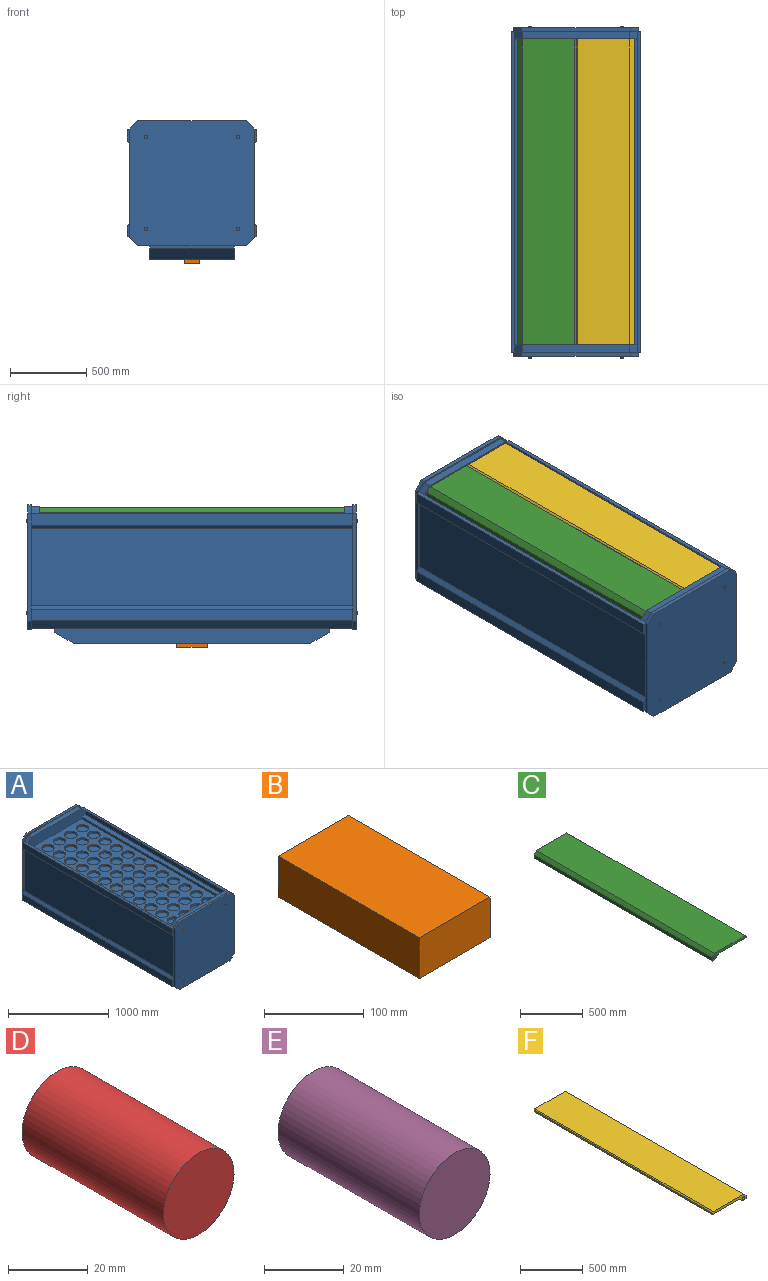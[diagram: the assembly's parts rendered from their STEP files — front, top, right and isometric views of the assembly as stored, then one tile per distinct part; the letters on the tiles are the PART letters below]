
ASSEMBLY  parts=6 mates=5
PART A: 218 faces, bbox 850x2170x910 mm
  f0: plane 1540.19x550mm, normal (0,0,-1), area 827105.8mm2, adj f28,f29,f30,f129,f213,f214,f215,f216
  f1: plane 820x60mm, normal (0,1,0), area 8579.9mm2, adj f11,f13,f14,f15,f16,f65,f122,f123
  f2: plane 520x10mm, normal (0,-1,0), area 5100mm2, adj f5,f24,f67,f68
  f3: plane 520x10mm, normal (0,1,0), area 5100mm2, adj f5,f16,f67,f68
  f4: plane 820x60mm, normal (0,-1,0), area 8579.9mm2, adj f10,f12,f22,f23,f24,f61,f121,f126
  f5: plane 2100x500mm, normal (1,0,0), area 1050000mm2, adj f2,f3,f67,f68
  f6: plane 700x50mm, normal (0,0,1), area 35000mm2, adj f7,f19,f53,f120
  f7: plane 50x50mm, normal (0.71,0,0.71), area 3535.5mm2, adj f6,f19,f53,f61
  f8: plane 820x820mm, normal (0,1,0), area 664559.8mm2, adj f21,f22,f23,f24,f25,f41,f42,f43
  f9: plane 820x820mm, normal (0,-1,0), area 664559.8mm2, adj f14,f15,f16,f17,f18,f31,f32,f33
  f10: plane 700x50mm, normal (0,0,1), area 35000mm2, adj f4,f12,f51,f121
  f11: plane 2100x700mm, normal (0,0,-1), area 480000mm2, adj f1,f13,f20,f26,f27,f28,f122,f129
  f12: plane 50x50mm, normal (0.71,0,0.71), area 3535.5mm2, adj f4,f10,f51,f61
  f13: plane 2100x50mm, normal (0.71,0,-0.71), area 148492.4mm2, adj f1,f11,f20,f65
  f14: plane 708.28x25mm, normal (0,0,-1), area 17707.1mm2, adj f1,f9,f15,f123
  f15: plane 55.86x55.86mm, normal (0.71,0,-0.71), area 1974.9mm2, adj f1,f9,f14,f16
  f16: plane 708.28x25mm, normal (1,0,0), area 17707.1mm2, adj f1,f3,f9,f15,f17,f19,f58,f64
  f17: plane 55.86x55.86mm, normal (0.71,0,0.71), area 1974.9mm2, adj f9,f16,f18,f19
  f18: plane 708.28x25mm, normal (0,0,1), area 17707.1mm2, adj f9,f17,f19,f125
  f19: plane 820x60mm, normal (0,1,0), area 8579.9mm2, adj f6,f7,f16,f17,f18,f61,f120,f124
  f20: plane 820x60mm, normal (0,-1,0), area 8579.9mm2, adj f11,f13,f21,f24,f25,f65,f122,f127
  f21: plane 708.28x25mm, normal (0,0,-1), area 17707.1mm2, adj f8,f20,f25,f128
  f22: plane 708.28x25mm, normal (0,0,1), area 17707.1mm2, adj f4,f8,f23,f126
  f23: plane 55.86x55.86mm, normal (0.71,0,0.71), area 1974.9mm2, adj f4,f8,f22,f24
  f24: plane 708.28x25mm, normal (1,0,0), area 17707.1mm2, adj f2,f4,f8,f20,f23,f25,f59,f63
  f25: plane 55.86x55.86mm, normal (0.71,0,-0.71), area 1974.9mm2, adj f8,f20,f21,f24
  f26: plane 550x25mm, normal (0,-1,0), area 13750mm2, adj f11,f28,f30,f129
  f27: plane 550x25mm, normal (0,1,0), area 13750mm2, adj f11,f28,f29,f129
  f28: plane 1800x100mm, normal (1,0,0), area 170257.2mm2, adj f0,f11,f26,f27,f29,f30
  f29: plane 550x129.9mm, normal (0,0.5,-0.87), area 82500mm2, adj f0,f27,f28,f129
  f30: plane 550x129.9mm, normal (0,-0.5,-0.87), area 82500mm2, adj f0,f26,f28,f129
  f31: plane 20x10mm, normal (0,0,1), area 200mm2, adj f9,f32,f34,f35
  f32: plane 20x10mm, normal (-1,0,0), area 200mm2, adj f9,f31,f33,f35
  f33: plane 20x10mm, normal (0,0,-1), area 200mm2, adj f9,f32,f34,f35
  f34: plane 20x10mm, normal (1,0,0), area 200mm2, adj f9,f31,f33,f35
  f35: plane 20x20mm, normal (0,-1,0), area 400mm2, adj f31,f32,f33,f34
  f36: plane 20x10mm, normal (0,0,1), area 200mm2, adj f9,f37,f39,f40
  f37: plane 20x10mm, normal (-1,0,0), area 200mm2, adj f9,f36,f38,f40
  f38: plane 20x10mm, normal (0,0,-1), area 200mm2, adj f9,f37,f39,f40
  f39: plane 20x10mm, normal (1,0,0), area 200mm2, adj f9,f36,f38,f40
  f40: plane 20x20mm, normal (0,-1,0), area 400mm2, adj f36,f37,f38,f39
  f41: plane 20x10mm, normal (0,0,1), area 200mm2, adj f8,f42,f44,f45
  f42: plane 20x10mm, normal (1,0,0), area 200mm2, adj f8,f41,f43,f45
  f43: plane 20x10mm, normal (0,0,-1), area 200mm2, adj f8,f42,f44,f45
  f44: plane 20x10mm, normal (-1,0,0), area 200mm2, adj f8,f41,f43,f45
  f45: plane 20x20mm, normal (0,1,0), area 400mm2, adj f41,f42,f43,f44
  f46: plane 20x10mm, normal (0,0,1), area 200mm2, adj f8,f47,f49,f50
  f47: plane 20x10mm, normal (1,0,0), area 200mm2, adj f8,f46,f48,f50
  f48: plane 20x10mm, normal (0,0,-1), area 200mm2, adj f8,f47,f49,f50
  f49: plane 20x10mm, normal (-1,0,0), area 200mm2, adj f8,f46,f48,f50
  f50: plane 20x20mm, normal (0,1,0), area 400mm2, adj f46,f47,f48,f49
  f51: plane 800x125mm, normal (0,-1,0), area 95000mm2, adj f10,f12,f52,f54,f55,f60,f121,f150
  f52: plane 2000x50mm, normal (0,0,1), area 100000mm2, adj f51,f53,f54,f60
  f53: plane 800x125mm, normal (0,1,0), area 94018.3mm2, adj f6,f7,f52,f54,f55,f56,f60,f120
  f54: plane 2000x25mm, normal (-1,0,0), area 50000mm2, adj f51,f52,f53,f55
  f55: plane 2000x700mm, normal (0,0,1), area 810951.4mm2, adj f51,f53,f54,f69,f71,f73,f75,f77
  f56: cylinder r=12.5mm len=25mm, axis (0,1,0), area 1963.5mm2, adj f53,f57
  f57: plane 25x25mm, normal (0,1,0), area 490.9mm2, adj f56
  f58: plane 90x15mm, normal (0,-1,0), area 1237.5mm2, adj f16,f61,f62,f68
  f59: plane 90x15mm, normal (0,1,0), area 1237.5mm2, adj f24,f61,f62,f68
  f60: plane 2000x50mm, normal (-1,0,0), area 100000mm2, adj f51,f52,f53,f61
  f61: plane 2100x25mm, normal (0,0,1), area 52500mm2, adj f4,f7,f12,f19,f58,f59,f60,f62
  f62: plane 2100x75mm, normal (1,0,0), area 157500mm2, adj f58,f59,f61,f68
  f63: plane 90x15mm, normal (0,1,0), area 1237.5mm2, adj f24,f65,f66,f67
  f64: plane 90x15mm, normal (0,-1,0), area 1237.5mm2, adj f16,f65,f66,f67
  f65: plane 2100x25mm, normal (0,0,-1), area 52500mm2, adj f1,f13,f20,f63,f64,f66
  f66: plane 2100x75mm, normal (1,0,0), area 157500mm2, adj f63,f64,f65,f67
  f67: plane 2100x25mm, normal (0.71,0,0.71), area 74246.2mm2, adj f2,f3,f5,f63,f64,f66
  f68: plane 2100x25mm, normal (0.71,0,-0.71), area 74246.2mm2, adj f2,f3,f5,f58,f59,f62
  f69: cylinder r=62.5mm len=125mm, axis (0,0,1), area 9817.5mm2, adj f55,f70
  f70: plane 125x125mm, normal (0,0,1), area 12271.8mm2, adj f69
  f71: cylinder r=62.5mm len=125mm, axis (0,0,1), area 9817.5mm2, adj f55,f72
  f72: plane 125x125mm, normal (0,0,1), area 12271.8mm2, adj f71
  f73: cylinder r=62.5mm len=125mm, axis (0,0,1), area 9817.5mm2, adj f55,f74
  f74: plane 125x125mm, normal (0,0,1), area 12271.8mm2, adj f73
  f75: cylinder r=62.5mm len=125mm, axis (0,0,1), area 9817.5mm2, adj f55,f76
  f76: plane 125x125mm, normal (0,0,1), area 12271.8mm2, adj f75
  f77: cylinder r=62.5mm len=125mm, axis (0,0,1), area 9817.5mm2, adj f55,f78
  f78: plane 125x125mm, normal (0,0,1), area 12271.8mm2, adj f77
  f79: cylinder r=62.5mm len=125mm, axis (0,0,1), area 9817.5mm2, adj f55,f80
  f80: plane 125x125mm, normal (0,0,1), area 12271.8mm2, adj f79
  f81: cylinder r=62.5mm len=125mm, axis (0,0,1), area 9817.5mm2, adj f55,f82
  f82: plane 125x125mm, normal (0,0,1), area 12271.8mm2, adj f81
  f83: cylinder r=62.5mm len=125mm, axis (0,0,1), area 9817.5mm2, adj f55,f84
  f84: plane 125x125mm, normal (0,0,1), area 12271.8mm2, adj f83
  f85: cylinder r=62.5mm len=125mm, axis (0,0,1), area 9817.5mm2, adj f55,f86
  f86: plane 125x125mm, normal (0,0,1), area 12271.8mm2, adj f85
  f87: cylinder r=62.5mm len=125mm, axis (0,0,1), area 9817.5mm2, adj f55,f88
  f88: plane 125x125mm, normal (0,0,1), area 12271.8mm2, adj f87
  f89: cylinder r=62.5mm len=125mm, axis (0,0,1), area 9817.5mm2, adj f55,f90
  f90: plane 125x125mm, normal (0,0,1), area 12271.8mm2, adj f89
  f91: cylinder r=62.5mm len=125mm, axis (0,0,1), area 9817.5mm2, adj f55,f92
  f92: plane 125x125mm, normal (0,0,1), area 12271.8mm2, adj f91
  f93: cylinder r=62.5mm len=125mm, axis (0,0,1), area 9817.5mm2, adj f55,f94
  f94: plane 125x125mm, normal (0,0,1), area 12271.8mm2, adj f93
  f95: cylinder r=62.5mm len=125mm, axis (0,0,1), area 9817.5mm2, adj f55,f96
  f96: plane 125x125mm, normal (0,0,1), area 12271.8mm2, adj f95
  f97: cylinder r=62.5mm len=125mm, axis (0,0,1), area 9817.5mm2, adj f55,f98
  f98: plane 125x125mm, normal (0,0,1), area 12271.8mm2, adj f97
  f99: cylinder r=62.5mm len=125mm, axis (0,0,1), area 9817.5mm2, adj f55,f100
  f100: plane 125x125mm, normal (0,0,1), area 12271.8mm2, adj f99
  f101: cylinder r=62.5mm len=125mm, axis (0,0,1), area 9817.5mm2, adj f55,f102
  f102: plane 125x125mm, normal (0,0,1), area 12271.8mm2, adj f101
  f103: cylinder r=62.5mm len=125mm, axis (0,0,1), area 9817.5mm2, adj f55,f104
  f104: plane 125x125mm, normal (0,0,1), area 12271.8mm2, adj f103
  f105: cylinder r=62.5mm len=125mm, axis (0,0,1), area 9817.5mm2, adj f55,f106
  f106: plane 125x125mm, normal (0,0,1), area 12271.8mm2, adj f105
  f107: cylinder r=62.5mm len=125mm, axis (0,0,1), area 9817.5mm2, adj f55,f108
  f108: plane 125x125mm, normal (0,0,1), area 12271.8mm2, adj f107
  f109: cylinder r=62.5mm len=125mm, axis (0,0,1), area 9817.5mm2, adj f55,f110
  f110: plane 125x125mm, normal (0,0,1), area 12271.8mm2, adj f109
  f111: cylinder r=62.5mm len=125mm, axis (0,0,1), area 9817.5mm2, adj f55,f112
  f112: plane 125x125mm, normal (0,0,1), area 12271.8mm2, adj f111
  f113: cylinder r=62.5mm len=125mm, axis (0,0,1), area 9817.5mm2, adj f55,f114
  f114: plane 125x125mm, normal (0,0,1), area 12271.8mm2, adj f113
  f115: cylinder r=62.5mm len=125mm, axis (0,0,1), area 9817.5mm2, adj f55,f116
  f116: plane 125x125mm, normal (0,0,1), area 12271.8mm2, adj f115
  f117: plane 520x10mm, normal (0,-1,0), area 5100mm2, adj f119,f127,f163,f164
  f118: plane 520x10mm, normal (0,1,0), area 5100mm2, adj f119,f124,f163,f164
  f119: plane 2100x500mm, normal (-1,0,0), area 1050000mm2, adj f117,f118,f163,f164
  f120: plane 50x50mm, normal (-0.71,0,0.71), area 3535.5mm2, adj f6,f19,f53,f157
  f121: plane 50x50mm, normal (-0.71,0,0.71), area 3535.5mm2, adj f4,f10,f51,f157
  f122: plane 2100x50mm, normal (-0.71,0,-0.71), area 148492.4mm2, adj f1,f11,f20,f161
  f123: plane 55.86x55.86mm, normal (-0.71,0,-0.71), area 1974.9mm2, adj f1,f9,f14,f124
  f124: plane 708.28x25mm, normal (-1,0,0), area 17707.1mm2, adj f1,f9,f19,f118,f123,f125,f154,f160
  f125: plane 55.86x55.86mm, normal (-0.71,0,0.71), area 1974.9mm2, adj f9,f18,f19,f124
  f126: plane 55.86x55.86mm, normal (-0.71,0,0.71), area 1974.9mm2, adj f4,f8,f22,f127
  f127: plane 708.28x25mm, normal (-1,0,0), area 17707.1mm2, adj f4,f8,f20,f117,f126,f128,f155,f159
  f128: plane 55.86x55.86mm, normal (-0.71,0,-0.71), area 1974.9mm2, adj f8,f20,f21,f127
  f129: plane 1800x100mm, normal (-1,0,0), area 170257.2mm2, adj f0,f11,f26,f27,f29,f30
  f130: plane 20x10mm, normal (0,0,1), area 200mm2, adj f9,f131,f133,f134
  f131: plane 20x10mm, normal (1,0,0), area 200mm2, adj f9,f130,f132,f134
  f132: plane 20x10mm, normal (0,0,-1), area 200mm2, adj f9,f131,f133,f134
  f133: plane 20x10mm, normal (-1,0,0), area 200mm2, adj f9,f130,f132,f134
  f134: plane 20x20mm, normal (0,-1,0), area 400mm2, adj f130,f131,f132,f133
  f135: plane 20x10mm, normal (0,0,1), area 200mm2, adj f9,f136,f138,f139
  f136: plane 20x10mm, normal (1,0,0), area 200mm2, adj f9,f135,f137,f139
  f137: plane 20x10mm, normal (0,0,-1), area 200mm2, adj f9,f136,f138,f139
  f138: plane 20x10mm, normal (-1,0,0), area 200mm2, adj f9,f135,f137,f139
  f139: plane 20x20mm, normal (0,-1,0), area 400mm2, adj f135,f136,f137,f138
  f140: plane 20x10mm, normal (0,0,1), area 200mm2, adj f8,f141,f143,f144
  f141: plane 20x10mm, normal (-1,0,0), area 200mm2, adj f8,f140,f142,f144
  f142: plane 20x10mm, normal (0,0,-1), area 200mm2, adj f8,f141,f143,f144
  f143: plane 20x10mm, normal (1,0,0), area 200mm2, adj f8,f140,f142,f144
  f144: plane 20x20mm, normal (0,1,0), area 400mm2, adj f140,f141,f142,f143
  f145: plane 20x10mm, normal (0,0,1), area 200mm2, adj f8,f146,f148,f149
  f146: plane 20x10mm, normal (-1,0,0), area 200mm2, adj f8,f145,f147,f149
  f147: plane 20x10mm, normal (0,0,-1), area 200mm2, adj f8,f146,f148,f149
  f148: plane 20x10mm, normal (1,0,0), area 200mm2, adj f8,f145,f147,f149
  f149: plane 20x20mm, normal (0,1,0), area 400mm2, adj f145,f146,f147,f148
  f150: plane 2000x50mm, normal (0,0,1), area 100000mm2, adj f51,f53,f151,f156
  f151: plane 2000x25mm, normal (1,0,0), area 50000mm2, adj f51,f53,f55,f150
  f152: cylinder r=12.5mm len=25mm, axis (0,1,0), area 1963.5mm2, adj f53,f153
  f153: plane 25x25mm, normal (0,1,0), area 490.9mm2, adj f152
  f154: plane 90x15mm, normal (0,-1,0), area 1237.5mm2, adj f124,f157,f158,f164
  f155: plane 90x15mm, normal (0,1,0), area 1237.5mm2, adj f127,f157,f158,f164
  f156: plane 2000x50mm, normal (1,0,0), area 100000mm2, adj f51,f53,f150,f157
  f157: plane 2100x25mm, normal (0,0,1), area 52500mm2, adj f4,f19,f120,f121,f154,f155,f156,f158
  f158: plane 2100x75mm, normal (-1,0,0), area 157500mm2, adj f154,f155,f157,f164
  f159: plane 90x15mm, normal (0,1,0), area 1237.5mm2, adj f127,f161,f162,f163
  f160: plane 90x15mm, normal (0,-1,0), area 1237.5mm2, adj f124,f161,f162,f163
  f161: plane 2100x25mm, normal (0,0,-1), area 52500mm2, adj f1,f20,f122,f159,f160,f162
  f162: plane 2100x75mm, normal (-1,0,0), area 157500mm2, adj f159,f160,f161,f163
  f163: plane 2100x25mm, normal (-0.71,0,0.71), area 74246.2mm2, adj f117,f118,f119,f159,f160,f162
  f164: plane 2100x25mm, normal (-0.71,0,-0.71), area 74246.2mm2, adj f117,f118,f119,f154,f155,f158
  f165: cylinder r=62.5mm len=125mm, axis (0,0,1), area 9817.5mm2, adj f55,f166
  f166: plane 125x125mm, normal (0,0,1), area 12271.8mm2, adj f165
  f167: cylinder r=62.5mm len=125mm, axis (0,0,1), area 9817.5mm2, adj f55,f168
  f168: plane 125x125mm, normal (0,0,1), area 12271.8mm2, adj f167
  f169: cylinder r=62.5mm len=125mm, axis (0,0,1), area 9817.5mm2, adj f55,f170
  f170: plane 125x125mm, normal (0,0,1), area 12271.8mm2, adj f169
  f171: cylinder r=62.5mm len=125mm, axis (0,0,1), area 9817.5mm2, adj f55,f172
  f172: plane 125x125mm, normal (0,0,1), area 12271.8mm2, adj f171
  f173: cylinder r=62.5mm len=125mm, axis (0,0,1), area 9817.5mm2, adj f55,f174
  f174: plane 125x125mm, normal (0,0,1), area 12271.8mm2, adj f173
  f175: cylinder r=62.5mm len=125mm, axis (0,0,1), area 9817.5mm2, adj f55,f176
  f176: plane 125x125mm, normal (0,0,1), area 12271.8mm2, adj f175
  f177: cylinder r=62.5mm len=125mm, axis (0,0,1), area 9817.5mm2, adj f55,f178
  f178: plane 125x125mm, normal (0,0,1), area 12271.8mm2, adj f177
  f179: cylinder r=62.5mm len=125mm, axis (0,0,1), area 9817.5mm2, adj f55,f180
  f180: plane 125x125mm, normal (0,0,1), area 12271.8mm2, adj f179
  f181: cylinder r=62.5mm len=125mm, axis (0,0,1), area 9817.5mm2, adj f55,f182
  f182: plane 125x125mm, normal (0,0,1), area 12271.8mm2, adj f181
  f183: cylinder r=62.5mm len=125mm, axis (0,0,1), area 9817.5mm2, adj f55,f184
  f184: plane 125x125mm, normal (0,0,1), area 12271.8mm2, adj f183
  f185: cylinder r=62.5mm len=125mm, axis (0,0,1), area 9817.5mm2, adj f55,f186
  f186: plane 125x125mm, normal (0,0,1), area 12271.8mm2, adj f185
  f187: cylinder r=62.5mm len=125mm, axis (0,0,1), area 9817.5mm2, adj f55,f188
  f188: plane 125x125mm, normal (0,0,1), area 12271.8mm2, adj f187
  f189: cylinder r=62.5mm len=125mm, axis (0,0,1), area 9817.5mm2, adj f55,f190
  f190: plane 125x125mm, normal (0,0,1), area 12271.8mm2, adj f189
  f191: cylinder r=62.5mm len=125mm, axis (0,0,1), area 9817.5mm2, adj f55,f192
  f192: plane 125x125mm, normal (0,0,1), area 12271.8mm2, adj f191
  f193: cylinder r=62.5mm len=125mm, axis (0,0,1), area 9817.5mm2, adj f55,f194
  f194: plane 125x125mm, normal (0,0,1), area 12271.8mm2, adj f193
  f195: cylinder r=62.5mm len=125mm, axis (0,0,1), area 9817.5mm2, adj f55,f196
  f196: plane 125x125mm, normal (0,0,1), area 12271.8mm2, adj f195
  f197: cylinder r=62.5mm len=125mm, axis (0,0,1), area 9817.5mm2, adj f55,f198
  f198: plane 125x125mm, normal (0,0,1), area 12271.8mm2, adj f197
  f199: cylinder r=62.5mm len=125mm, axis (0,0,1), area 9817.5mm2, adj f55,f200
  f200: plane 125x125mm, normal (0,0,1), area 12271.8mm2, adj f199
  f201: cylinder r=62.5mm len=125mm, axis (0,0,1), area 9817.5mm2, adj f55,f202
  f202: plane 125x125mm, normal (0,0,1), area 12271.8mm2, adj f201
  f203: cylinder r=62.5mm len=125mm, axis (0,0,1), area 9817.5mm2, adj f55,f204
  f204: plane 125x125mm, normal (0,0,1), area 12271.8mm2, adj f203
  f205: cylinder r=62.5mm len=125mm, axis (0,0,1), area 9817.5mm2, adj f55,f206
  f206: plane 125x125mm, normal (0,0,1), area 12271.8mm2, adj f205
  f207: cylinder r=62.5mm len=125mm, axis (0,0,1), area 9817.5mm2, adj f55,f208
  f208: plane 125x125mm, normal (0,0,1), area 12271.8mm2, adj f207
  f209: cylinder r=62.5mm len=125mm, axis (0,0,1), area 9817.5mm2, adj f55,f210
  f210: plane 125x125mm, normal (0,0,1), area 12271.8mm2, adj f209
  f211: cylinder r=62.5mm len=125mm, axis (0,0,1), area 9817.5mm2, adj f55,f212
  f212: plane 125x125mm, normal (0,0,1), area 12271.8mm2, adj f211
  f213: plane 100x25mm, normal (0,1,0), area 2500mm2, adj f0,f214,f216,f217
  f214: plane 200x25mm, normal (1,0,0), area 5000mm2, adj f0,f213,f215,f217
  f215: plane 100x25mm, normal (0,-1,0), area 2500mm2, adj f0,f214,f216,f217
  f216: plane 200x25mm, normal (-1,0,0), area 5000mm2, adj f0,f213,f215,f217
  f217: plane 200x100mm, normal (0,0,-1), area 20000mm2, adj f213,f214,f215,f216
PART B: 6 faces, bbox 100x200x50 mm
  f0: plane 100x50mm, normal (0,-1,0), area 5000mm2, adj f1,f3,f4,f5
  f1: plane 200x50mm, normal (-1,0,0), area 10000mm2, adj f0,f2,f4,f5
  f2: plane 100x50mm, normal (0,1,0), area 5000mm2, adj f1,f3,f4,f5
  f3: plane 200x50mm, normal (1,0,0), area 10000mm2, adj f0,f2,f4,f5
  f4: plane 200x100mm, normal (0,0,-1), area 20000mm2, adj f0,f1,f2,f3
  f5: plane 200x100mm, normal (0,0,1), area 20000mm2, adj f0,f1,f2,f3
PART C: 12 faces, bbox 380x2000x60 mm
  f0: plane 380x60mm, normal (0,-1,0), area 10521.6mm2, adj f1,f2,f3,f4,f5,f6,f7,f8
  f1: plane 2000x40mm, normal (0,0,-1), area 80000mm2, adj f0,f2,f6,f10
  f2: plane 2000x35mm, normal (0.71,0,-0.71), area 98994.9mm2, adj f0,f1,f3,f10
  f3: plane 2000x305mm, normal (0,0,-1), area 610000mm2, adj f0,f2,f4,f10
  f4: plane 2000x15mm, normal (1,0,0), area 30000mm2, adj f0,f3,f10,f11
  f5: cylinder r=12.5mm len=25mm, axis (0,1,0), area 1963.5mm2, adj f0,f9
  f6: plane 2000x30mm, normal (-1,0,0), area 60000mm2, adj f0,f1,f8,f10
  f7: plane 2000x340mm, normal (0,0,1), area 680000mm2, adj f0,f8,f10,f11
  f8: plane 2000x30mm, normal (-0.71,0,0.71), area 84852.8mm2, adj f0,f6,f7,f10
  f9: plane 25x25mm, normal (0,-1,0), area 490.9mm2, adj f5
  f10: plane 380x60mm, normal (0,1,0), area 11012.5mm2, adj f1,f2,f3,f4,f6,f7,f8,f11
  f11: plane 2000x10mm, normal (0.71,0,0.71), area 28284.3mm2, adj f0,f4,f7,f10
PART D: 3 faces, bbox 25x50x25 mm
  f0: cylinder r=12.5mm len=50mm, axis (0,-1,0), area 3927mm2, adj f1,f2
  f1: plane 25x25mm, normal (0,1,0), area 490.9mm2, adj f0
  f2: plane 25x25mm, normal (0,-1,0), area 490.9mm2, adj f0
PART E: 3 faces, bbox 25x50x25 mm
  f0: cylinder r=12.5mm len=50mm, axis (0,-1,0), area 3927mm2, adj f1,f2
  f1: plane 25x25mm, normal (0,1,0), area 490.9mm2, adj f0
  f2: plane 25x25mm, normal (0,-1,0), area 490.9mm2, adj f0
PART F: 12 faces, bbox 380x2000x60 mm
  f0: plane 380x60mm, normal (0,-1,0), area 10521.6mm2, adj f1,f2,f3,f4,f5,f6,f7,f8
  f1: plane 2000x40mm, normal (0,0,-1), area 80000mm2, adj f0,f2,f6,f10
  f2: plane 2000x35mm, normal (-0.71,0,-0.71), area 98994.9mm2, adj f0,f1,f3,f10
  f3: plane 2000x305mm, normal (0,0,-1), area 610000mm2, adj f0,f2,f4,f10
  f4: plane 2000x15mm, normal (-1,0,0), area 30000mm2, adj f0,f3,f10,f11
  f5: cylinder r=12.5mm len=25mm, axis (0,1,0), area 1963.5mm2, adj f0,f9
  f6: plane 2000x30mm, normal (1,0,0), area 60000mm2, adj f0,f1,f8,f10
  f7: plane 2000x340mm, normal (0,0,1), area 680000mm2, adj f0,f8,f10,f11
  f8: plane 2000x30mm, normal (0.71,0,0.71), area 84852.8mm2, adj f0,f6,f7,f10
  f9: plane 25x25mm, normal (0,-1,0), area 490.9mm2, adj f5
  f10: plane 380x60mm, normal (0,1,0), area 11012.5mm2, adj f1,f2,f3,f4,f6,f7,f8,f11
  f11: plane 2000x10mm, normal (-0.71,0,0.71), area 28284.3mm2, adj f0,f4,f7,f10
PLACE A t=(-25.34,-1050,140.7)mm
PLACE B t=(-25.34,-1050,140.7)mm
PLACE C t=(-25.34,-1050,140.7)mm
PLACE D t=(-25.34,-1050,140.7)mm
PLACE E t=(-25.34,-1050,140.7)mm
PLACE F t=(-25.34,-1050,140.7)mm
MATE fastened C.f5 <-> E.f0  axis (0,-1,0) through (-375.34,-975,890.7)mm
MATE revolute D.f0 <-> A.f56  axis (0,-1,0) through (324.66,-1025,890.7)mm
MATE fastened F.f5 <-> D.f0  axis (0,-1,0) through (324.66,-975,890.7)mm
MATE fastened B.f5 <-> A.f217  axis (0,0,1) through (-25.34,0,65.7)mm
MATE revolute E.f0 <-> A.f152  axis (0,-1,0) through (-375.34,-1025,890.7)mm
